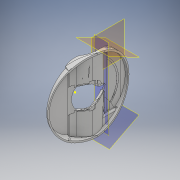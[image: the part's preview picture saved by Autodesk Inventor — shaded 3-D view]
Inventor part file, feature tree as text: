
AUTODESK INVENTOR PART (.ipt)
format: ipt  version: 2018 (Build 220112000, 112)  size: 2,058,240 bytes
history: native  units: mm
features: sketch x62, extrude x55, fillet x14, plane x4, revolve x1, mirror x1
ambient origin geometry x8: Origin, YZ Plane, XZ Plane, XY Plane, X Axis, Y Axis, Z Axis, Center Point
bodies: Solid1 (feature_tree)
feature tree (137):
  extrude  "Extrusion1"  TaperAngle=0.0deg  [1 undecoded]
  extrude  "Extrusion2"  Depth=10.0mm TaperAngle=0.0deg
  extrude  "Extrusion3"  Depth=50.0mm
  extrude  "Extrusion4"  TaperAngle=0.0deg  [1 undecoded]
  extrude  "Extrusion5"  Depth=10.0mm TaperAngle=0.0deg
  sketch  "Sketch6"  dims[d19=10.0mm d20=0.0mm d21=40.0mm]
  extrude  "Extrusion6"  Depth=40.0mm
  extrude  "Extrusion7"  Depth=11.0mm TaperAngle=0.0deg
  extrude  "Extrusion8"  Depth=32.0mm TaperAngle=0.0deg
  extrude  "Extrusion9"  Depth=32.0mm TaperAngle=0.0deg
  extrude  "Extrusion10"  Depth=10.0mm TaperAngle=0.0deg
  extrude  "Extrusion11"  Depth=10.0mm TaperAngle=0.0deg
  extrude  "Extrusion12"  TaperAngle=0.0deg  [1 undecoded]
  extrude  "Extrusion14"  Depth=48.3mm
  extrude  "Extrusion15"  TaperAngle=0.0deg  [1 undecoded]
  extrude  "Extrusion16"  Depth=10.0mm TaperAngle=0.0deg
  extrude  "Extrusion17"  Depth=11.63mm TaperAngle=0.0deg
  sketch  "Sketch21"  dims[d83=0.0mm d84=0.0mm d85=0.0mm d86=0.0mm]
  extrude  "Extrusion19"  Depth=11.63mm TaperAngle=0.0deg
  extrude  "Extrusion20"  TaperAngle=0.0deg  [1 undecoded]
  extrude  "Extrusion21"  Depth=10.0mm TaperAngle=0.0deg
  extrude  "Extrusion22"  TaperAngle=0.0deg  [1 undecoded]
  extrude  "Extrusion23"  Depth=2.86mm TaperAngle=0.0deg
  extrude  "Extrusion24"  TaperAngle=0.0deg  [1 undecoded]
  extrude  "Extrusion25"  Depth=2.22mm
  sketch  "Sketch33"  dims[d113=7.8mm d114=0.0mm d115=7.8mm d116=0.0mm]
  extrude  "Extrusion26"  Depth=10.0mm TaperAngle=0.0deg
  extrude  "Extrusion27"  Depth=7.8mm TaperAngle=0.0deg
  extrude  "Extrusion28"  Depth=16.0mm TaperAngle=0.0deg
  extrude  "Extrusion29"  Depth=22.0mm TaperAngle=0.0deg
  extrude  "Extrusion30"  Depth=17.0mm TaperAngle=0.0deg
  extrude  "Extrusion31"  Depth=2.0mm
  extrude  "Extrusion32"  Depth=6.95mm TaperAngle=0.0deg
  extrude  "Extrusion33"  Depth=18.0mm TaperAngle=0.0deg
  sketch  "Sketch42"  dims[d145=2.0mm d146=7.72mm d147=0.0mm]
  extrude  "Extrusion34"  Depth=1.02mm
  extrude  "Extrusion36"  Depth=15.5mm TaperAngle=0.0deg
  extrude  "Extrusion37"  Depth=7.72mm TaperAngle=0.0deg
  revolve  "Revolution3"  [1 undecoded]
  extrude  "Extrusion38"  Depth=2.0mm
  extrude  "Extrusion39"  Depth=2.0mm
  extrude  "Extrusion40"  Depth=2.0mm
  fillet  "Fillet1"  Radius=2.0mm
  fillet  "Fillet2"  [1 undecoded]
  sketch  "Sketch51"
  extrude  "Extrusion41"  [1 undecoded]
  mirror  "Mirror1"
  extrude  "Extrusion42"  [1 undecoded]
  sketch  "Sketch54"
  sketch  "Sketch55"
  sketch  "Sketch56"
  extrude  "Extrusion44"  [1 undecoded]
  extrude  "Extrusion45"  [1 undecoded]
  extrude  "Extrusion46"  [1 undecoded]
  extrude  "Extrusion47"  [1 undecoded]
  plane  "Work Plane2"
  extrude  "Extrusion48"  [1 undecoded]
  extrude  "Extrusion49"  [1 undecoded]
  plane  "Work Plane4"
  sketch  "Sketch64"
  plane  "Work Plane5"
  extrude  "Extrusion50"  [1 undecoded]
  extrude  "Extrusion51"  [1 undecoded]
  fillet  "Fillet3"  [1 undecoded]
  fillet  "Fillet4"  [1 undecoded]
  extrude  "Extrusion52"  [1 undecoded]
  extrude  "Extrusion53"  [1 undecoded]
  extrude  "Extrusion54"  [1 undecoded]
  extrude  "Extrusion55"  [1 undecoded]
  fillet  "Fillet5"  [1 undecoded]
  extrude  "Extrusion56"  [1 undecoded]
  extrude  "Extrusion57"  [1 undecoded]
  fillet  "Fillet6"  [1 undecoded]
  extrude  "Extrusion58"  [1 undecoded]
  extrude  "Extrusion59"  [1 undecoded]
  fillet  "Fillet7"  [1 undecoded]
  fillet  "Fillet8"  [1 undecoded]
  fillet  "Fillet9"  [1 undecoded]
  fillet  "Fillet10"  [1 undecoded]
  fillet  "Fillet11"  [1 undecoded]
  fillet  "Fillet12"  [1 undecoded]
  fillet  "Fillet13"  [1 undecoded]
  fillet  "Fillet14"  [1 undecoded]
  sketch  "Sketch1"  dims[d0=10.0mm d1=0.0mm d2=0.0mm d3=0.0mm]
  sketch  "Sketch2"  dims[d4=0.0mm d5=0.0mm d6=10.0mm d7=0.0mm]
  sketch  "Sketch3"  dims[d8=10.0mm d9=0.0mm d10=50.0mm]
  sketch  "Sketch4"  dims[d11=10.0mm d12=0.0mm d13=0.0mm d14=0.0mm]
  sketch  "Sketch5"  dims[d15=0.0mm d16=0.0mm d17=10.0mm d18=0.0mm]
  sketch  "Sketch7"  dims[d22=38.0mm d23=11.0mm d24=0.0mm]
  sketch  "Sketch8"  dims[d25=9.5mm d26=0.0mm d33=32.0mm d34=0.0mm]
  sketch  "Sketch9"  dims[d37=32.0mm d38=0.0mm d39=32.0mm d40=0.0mm]
  sketch  "Sketch10"  dims[d41=32.0mm d42=0.0mm d45=10.0mm d46=0.0mm]
  sketch  "Sketch11"  dims[d47=10.0mm d48=0.0mm d49=10.0mm d50=0.0mm]
  sketch  "Sketch12"  dims[d51=0.0mm d52=0.0mm d53=0.0mm d54=0.0mm]
  sketch  "Sketch13"  dims[d65=46.0mm d66=48.3mm]
  sketch  "Sketch16"  dims[d67=9.0mm d68=0.0mm d69=0.0mm d70=0.0mm]
  sketch  "Sketch18"  dims[d71=0.0mm d72=0.0mm d73=10.0mm d74=0.0mm]
  sketch  "Sketch19"  dims[d75=5.0mm d76=0.0mm d77=11.63mm d78=0.0mm]
  sketch  "Sketch20"  dims[d79=11.63mm d80=0.0mm d81=11.63mm d82=0.0mm]
  sketch  "Sketch22"  dims[d87=30.0mm d88=10.0mm d89=0.0mm]
  sketch  "Sketch23"  dims[d92=10.0mm d93=0.0mm d94=0.0mm d95=0.0mm]
  sketch  "Sketch24"  dims[d96=135.0deg d99=2.86mm d100=0.0mm]
  sketch  "Sketch25"  dims[d101=0.0mm d102=0.0mm d103=0.0mm d104=0.0mm]
  sketch  "Sketch31"  dims[d105=2.01mm d106=2.22mm]
  sketch  "Sketch32"  dims[d107=10.0mm d108=0.0mm d109=10.0mm d110=0.0mm]
  sketch  "Sketch34"  dims[d117=0.0mm d118=0.0mm d119=16.0mm d120=0.0mm]
  sketch  "Sketch35"  dims[d121=22.0mm d122=0.0mm d123=22.0mm d124=0.0mm]
  sketch  "Sketch36"  dims[d125=90.0deg d126=17.0mm d127=0.0mm]
  sketch  "Sketch37"  dims[d128=17.0mm d129=0.0mm d130=2.0mm]
  sketch  "Sketch38"  dims[d131=2.0mm d132=6.95mm d133=0.0mm]
  sketch  "Sketch39"  dims[d134=6.95mm d135=0.0mm d136=18.0mm d137=0.0mm]
  sketch  "Sketch40"  dims[d138=16.0mm d139=0.0mm d140=1.02mm]
  sketch  "Sketch41"  dims[d141=1.0mm d142=0.0mm d143=15.5mm d144=0.0mm]
  sketch  "Sketch43"  dims[d148=17.0mm d149=0.0mm d150=2.0mm]
  sketch  "Sketch45"  dims[d151=2.0mm d152=2.0mm]
  sketch  "Sketch47"  dims[d153=2.0mm d154=2.0mm]
  sketch  "Sketch48"  dims[d155=2.0mm d156=2.0mm d157=2.0mm]
  sketch  "Sketch49"
  sketch  "Sketch50"
  sketch  "Sketch52"
  sketch  "Sketch53"
  sketch  "Sketch57"
  sketch  "Sketch60"
  sketch  "Sketch61"
  sketch  "Sketch62"
  sketch  "Sketch63"
  plane  "Work Plane3"
  sketch  "Sketch65"
  sketch  "Sketch66"
  sketch  "Sketch67"
  sketch  "Sketch68"
  sketch  "Sketch69"
  sketch  "Sketch70"
  sketch  "Sketch71"
  sketch  "Sketch72"
  sketch  "Sketch73"
  sketch  "Sketch74"
note: 39 required parameter values undecoded (feature->parameter linkage not recoverable at this tier; creation-order binding heuristic only, values carry confidence <= 0.55)